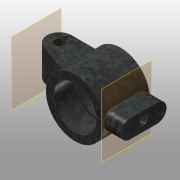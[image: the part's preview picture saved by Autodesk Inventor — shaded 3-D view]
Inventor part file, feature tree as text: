
AUTODESK INVENTOR PART (.ipt)
format: ipt  version: 2016 (Build 200138000, 138)  size: 193,024 bytes
history: native  units: mm
features: sketch x8, extrude x6, hole x3, plane x2, projected_geometry x1
ambient origin geometry x8: Origin, YZ Plane, XZ Plane, XY Plane, X Axis, Y Axis, Z Axis, Center Point
bodies: Solid1 (feature_tree)
feature tree (20):
  extrude  "Extrusion1"  Depth=15.0mm TaperAngle=0.0deg
  extrude  "Extrusion2"  Depth=7.0mm TaperAngle=0.0deg
  extrude  "Extrusion3"  Depth=7.0mm TaperAngle=0.0deg
  extrude  "Extrusion4"  Depth=21.5mm TaperAngle=0.0deg
  plane  "Work Plane1"
  extrude  "Extrusion5"  Depth=5.5mm TaperAngle=0.0deg
  extrude  "Extrusion6"  Depth=4.0mm
  hole  "Hole1"  [1 undecoded]
  hole  "Hole2"  [1 undecoded]
  plane  "Work Plane2"
  hole  "Hole3"  [1 undecoded]
  sketch  "Sketch1"  dims[d0=19.0mm d1=15.0mm d2=0.0mm]
  sketch  "Sketch2"  dims[d3=14.0mm d4=7.0mm d5=0.0mm]
  sketch  "Sketch3"  dims[d6=14.0mm d7=7.0mm d8=0.0mm]
  sketch  "Sketch5"  dims[d9=12.0mm d10=21.5mm d11=0.0mm]
  sketch  "Sketch6"  dims[d13=3.0mm d14=5.5mm d15=0.0mm]
  sketch  "Sketch7"  dims[d16=1.25mm d17=0.0mm d18=4.0mm]
  sketch  "Sketch8"  dims[d19=3.490659mm d21=16.15mm]
  sketch  "Sketch9"  dims[d22=10.0mm d23=0.0mm d49=10.0mm d50=10.0mm d26=3.1mm d27=6.0mm d28=4.0mm d29=2.0mm d30=90.0deg d31=17.3mm d32=20.594885mm d33=2.459mm d34=4.0mm d35=4.0mm d36=2.0mm d37=90.0deg d38=6.0mm d39=20.594885mm d40=2.459mm d41=4.0mm d42=4.0mm d43=2.0mm d44=90.0deg d45=4.0mm d46=20.594885mm]
  projected_geometry  "Project Cut Edges1"
note: 3 required parameter values undecoded (feature->parameter linkage not recoverable at this tier; creation-order binding heuristic only, values carry confidence <= 0.55)
